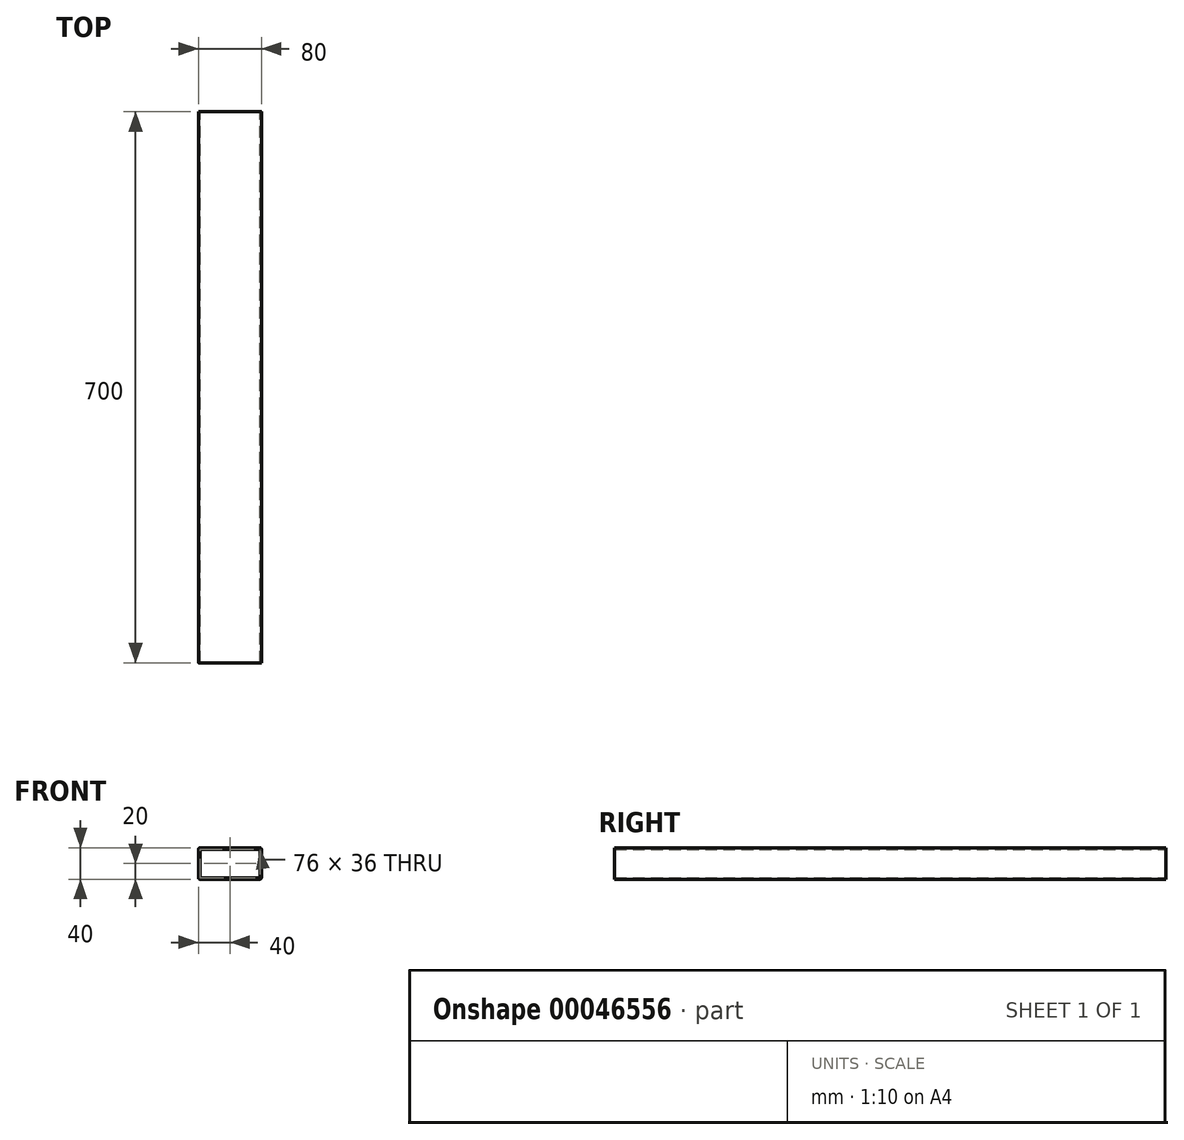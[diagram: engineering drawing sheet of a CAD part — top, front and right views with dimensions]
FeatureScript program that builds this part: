
annotation { "Feature Type Name" : "Feature", "Feature Type Description" : "" }
export const myFeature = defineFeature(function(context is Context, id is Id, definition is map)
    precondition{}
    {
        {
            var Q0;
            Q0=qCreatedBy(makeId("Front.planeOp"),FACE);
            var sketch = newSketch(context, id + "F0", { "sketchPlane" : qUnion([Q0])});
            skLineSegment(sketch, "E0", {"start": v(38, 18) * mm, "end": v(38, -18) * mm});
            skLineSegment(sketch, "E1", {"start": v(-38, 18) * mm, "end": v(38, 18) * mm});
            skLineSegment(sketch, "E2", {"start": v(-38, -18) * mm, "end": v(-38, 18) * mm});
            skLineSegment(sketch, "E3", {"start": v(38, -18) * mm, "end": v(-38, -18) * mm});
            skLineSegment(sketch, "E4", {"start": v(-40, 18) * mm, "end": v(-40, -18) * mm});
            skArc(sketch, "E5", {"start": v(-38, 20) * mm, "mid": v(-39.41, 19.41) * mm, "end": v(-40, 18) * mm});
            skLineSegment(sketch, "E6", {"start": v(38, 20) * mm, "end": v(-38, 20) * mm});
            skArc(sketch, "E7", {"start": v(40, 18) * mm, "mid": v(39.41, 19.41) * mm, "end": v(38, 20) * mm});
            skLineSegment(sketch, "E8", {"start": v(40, -18) * mm, "end": v(40, 18) * mm});
            skArc(sketch, "E9", {"start": v(38, -20) * mm, "mid": v(39.41, -19.41) * mm, "end": v(40, -18) * mm});
            skLineSegment(sketch, "E10", {"start": v(-38, -20) * mm, "end": v(38, -20) * mm});
            skArc(sketch, "E11", {"start": v(-40, -18) * mm, "mid": v(-39.41, -19.41) * mm, "end": v(-38, -20) * mm});
            skSolve(sketch);
        }
        {
            var Q0;
            Q0 = qSketchRegion(id + "F0", true);
            extrude(context, id + "F1", {"entities" : qUnion([Q0]), "depth" : 700 * mm});
        }
    });
